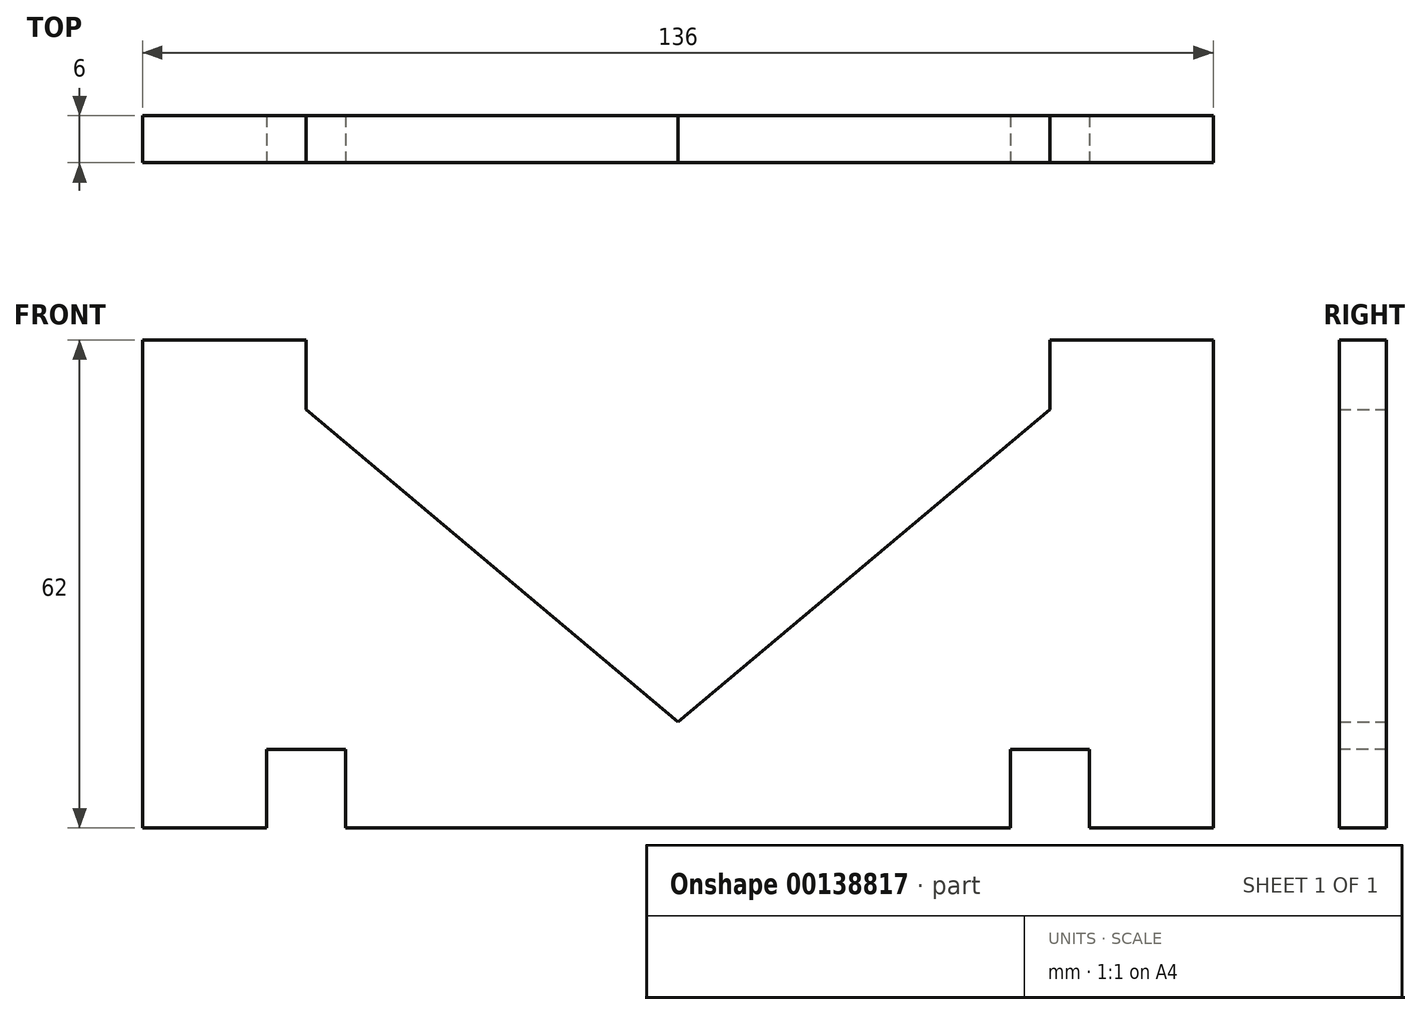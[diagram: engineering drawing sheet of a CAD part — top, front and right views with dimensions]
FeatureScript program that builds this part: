
annotation { "Feature Type Name" : "Feature", "Feature Type Description" : "" }
export const myFeature = defineFeature(function(context is Context, id is Id, definition is map)
    precondition{}
    {
        {
            var Q0;
            Q0=qCreatedBy(makeId("Front.planeOp"),FACE);
            var sketch = newSketch(context, id + "F0", { "sketchPlane" : qUnion([Q0])});
            skLineSegment(sketch, "E0", {"start": v(0, 0) * mm, "end": v(0, 62) * mm, "construction": true});
            skLineSegment(sketch, "E1", {"start": v(0, 0) * mm, "end": v(-68, 0) * mm});
            skLineSegment(sketch, "E2", {"start": v(-68, 0) * mm, "end": v(-68, 62) * mm});
            skLineSegment(sketch, "E3", {"start": v(-68, 62) * mm, "end": v(-47.25, 62) * mm});
            skLineSegment(sketch, "E4", {"start": v(-47.25, 62) * mm, "end": v(-47.25, 53.15) * mm});
            skLineSegment(sketch, "E5", {"start": v(-47.25, 53.15) * mm, "end": v(0, 13.5) * mm});
            skLineSegment(sketch, "E6.MirrorCS", {"start": v(47.25, 53.15) * mm, "end": v(0, 13.5) * mm});
            skLineSegment(sketch, "E7.MirrorCS", {"start": v(0, 0) * mm, "end": v(68, 0) * mm});
            skLineSegment(sketch, "E8.MirrorCS", {"start": v(68, 0) * mm, "end": v(68, 62) * mm});
            skLineSegment(sketch, "E9.MirrorCS", {"start": v(68, 62) * mm, "end": v(47.25, 62) * mm});
            skLineSegment(sketch, "E10.MirrorCS", {"start": v(47.25, 62) * mm, "end": v(47.25, 53.15) * mm});
            skSolve(sketch);
        }
        {
            var Q0;
            Q0 = qSketchRegion(id + "F0", true);
            extrude(context, id + "F1", {"entities" : qUnion([Q0]), "depth" : 6 * mm});
        }
        {
            var Q0;
            Q0=makeQuery(id+"F1.opExtrude","CAP_FACE",FACE,{"disambiguationData":[OSD([sQuery(id+"F0.wireOp",EDGE,"E1"),sQuery(id+"F0.wireOp",EDGE,"E2"),sQuery(id+"F0.wireOp",EDGE,"E3"),sQuery(id+"F0.wireOp",EDGE,"E4"),sQuery(id+"F0.wireOp",EDGE,"E5"),sQuery(id+"F0.wireOp",EDGE,"E6.MirrorCS"),sQuery(id+"F0.wireOp",EDGE,"E7.MirrorCS"),sQuery(id+"F0.wireOp",EDGE,"E8.MirrorCS"),sQuery(id+"F0.wireOp",EDGE,"E9.MirrorCS"),sQuery(id+"F0.wireOp",EDGE,"E10.MirrorCS")])],"isStart":false});
            var sketch = newSketch(context, id + "F2", { "sketchPlane" : qUnion([Q0])});
            skLineSegment(sketch, "E11", {"start": v(-52.25, 0) * mm, "end": v(-52.25, 10) * mm, "construction": true});
            skLineSegment(sketch, "E12", {"start": v(-52.25, 10) * mm, "end": v(-42.25, 10) * mm, "construction": true});
            skLineSegment(sketch, "E13", {"start": v(-42.25, 10) * mm, "end": v(-42.25, 0) * mm, "construction": true});
            skLineSegment(sketch, "E14.bottom", {"start": v(-52.25, 10) * mm, "end": v(-42.25, 10) * mm});
            skLineSegment(sketch, "E14.top", {"start": v(-52.25, 0) * mm, "end": v(-42.25, 0) * mm});
            skLineSegment(sketch, "E14.left", {"start": v(-52.25, 10) * mm, "end": v(-52.25, 0) * mm});
            skLineSegment(sketch, "E14.right", {"start": v(-42.25, 10) * mm, "end": v(-42.25, 0) * mm});
            skLineSegment(sketch, "E15.MirrorCS", {"start": v(42.25, 10) * mm, "end": v(42.25, 0) * mm, "construction": true});
            skLineSegment(sketch, "E16.MirrorCS", {"start": v(52.25, 10) * mm, "end": v(42.25, 10) * mm, "construction": true});
            skLineSegment(sketch, "E17.MirrorCS", {"start": v(52.25, 0) * mm, "end": v(52.25, 10) * mm, "construction": true});
            skLineSegment(sketch, "E18.MirrorCS", {"start": v(52.25, 0) * mm, "end": v(42.25, 0) * mm});
            skLineSegment(sketch, "E19.bottom", {"start": v(52.25, 10) * mm, "end": v(42.25, 10) * mm});
            skLineSegment(sketch, "E19.left", {"start": v(52.25, 10) * mm, "end": v(52.25, 0) * mm});
            skLineSegment(sketch, "E19.right", {"start": v(42.25, 10) * mm, "end": v(42.25, 0) * mm});
            skSolve(sketch);
        }
        {
            var Q0;
            Q0 = qSketchRegion(id + "F2", true);
            extrude(context, id + "F3", {"entities" : qUnion([Q0]), "operationType" : NewBodyOperationType.REMOVE, "endBound" : BoundingType.THROUGH_ALL, "oppositeDirection" : true, "depth" : 25 * mm});
        }
    });
